# Revit family: ledposttop-p1-_33w-3000-as-d76_708000000100
name_source: partatom
category: Leuchten
revit_build: Autodesk Revit 2016 (Build: 20190508_0715(x64)
units: mm (PartAtom-declared; Revit-internal decimal feet)

## family parameters
Basisbauteil = Fläche
Beim Laden mit Abzugskörper schneiden = Nein
Bemaßung runder Anschluss = Durchmesser verwenden
Gemeinsam genutzt = Nein
Lichtquelle = Nein
Raumberechnungspunkt = Nein
Teiletyp = Normal

## types (1)
- LEDPostTop-P1- 33W-3000-AS-D76 (1 x LED, 4000 lm)
    Approval mark = CE, ENEC
    Beschreibung = Professional post-top solution with optimal light performance. Integrates well into existing landscape. Different optics to suit the application and reduce glare. Die casted aluminium body for optimal heat dissipation. IP66 and suitable for use on the coastal applications.
    CIE Flux Codes = 29 64 95 99 100
    Control Gear = Electronic ballast
    Height = 565 mm
    Hersteller = OPPLE
    Lamp Light Flux = 4000 lm
    Lamp count = 1
    Lampe = 1 x LED
    Length = 450 mm
    Luminous efficacy = 121 lm/W
    ModVariant = Nein
    Modell = 708000000100
    Mounting Place = Pole
    Mounting Type = Pole top
    Number of Poles = 1
    OnlyDefault = Ja
    Power Factor = 1
    Product Name = LEDPostTop-P1- 33W-3000-AS-D76
    Product group = Post Top
    ProductGroupID = 6100
    Protection Class = Protection class I
    Protection Degree = IP 66
    RLX_Detail_Level = 1
    RlxData = <blob elided: 187497 chars, md5=f41d2d8a>
    Scheinlast = 33 VA
    Socket = socket
    Standby Power = 0 W
    System Light Flux = 4000 lm
    System Power = 33 W
    Typenbild = postt.jpg
    Typenkommentare = Product without accessories
    URL = http://relux.com
    VarID = ---
    Voltage = 0 V
    Vorgabe-Ansicht = 1800 mm
    Weight = 0.00 kg
    Width = 0 mm  [stored 0 ft]

note: [stored X ft] marks values corroborated as IEEE doubles in the binary element streams (Revit-internal decimal feet)

## geometry (parser evidence)
native form markers: Blend x4, Sweep x11
no freeform markers — native parametric forms only
